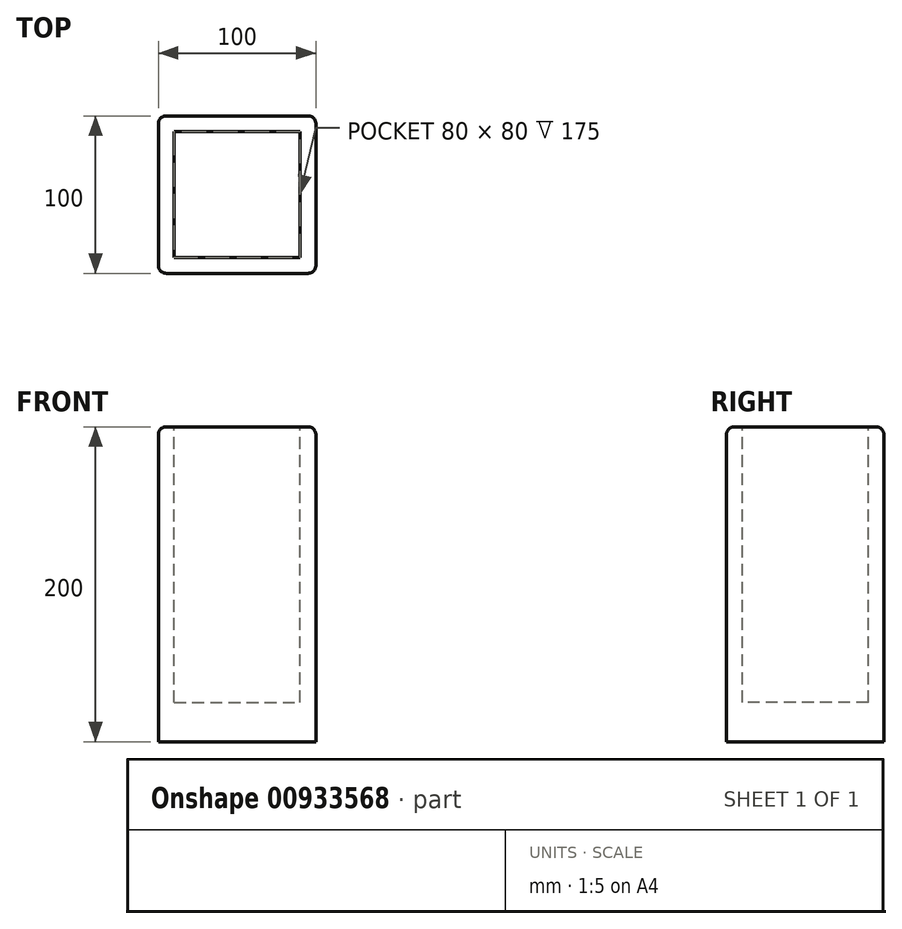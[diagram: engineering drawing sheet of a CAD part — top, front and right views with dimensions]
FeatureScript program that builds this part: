
annotation { "Feature Type Name" : "Feature", "Feature Type Description" : "" }
export const myFeature = defineFeature(function(context is Context, id is Id, definition is map)
    precondition{}
    {
        {
            var Q0;
            Q0=qCreatedBy(makeId("Top.planeOp"),FACE);
            var sketch = newSketch(context, id + "F0", { "sketchPlane" : qUnion([Q0])});
            skLineSegment(sketch, "E0.bottom", {"start": v(-50, 50) * mm, "end": v(50, 50) * mm});
            skLineSegment(sketch, "E0.top", {"start": v(-50, -50) * mm, "end": v(50, -50) * mm});
            skLineSegment(sketch, "E0.left", {"start": v(-50, 50) * mm, "end": v(-50, -50) * mm});
            skLineSegment(sketch, "E0.right", {"start": v(50, 50) * mm, "end": v(50, -50) * mm});
            skSolve(sketch);
        }
        {
            var Q0;
            Q0 = qSketchRegion(id + "F0", true);
            var Q1;
            Q1=makeQuery(id+"F0.imprint","IMPRINT",FACE,{"disambiguationData":[TD([[makeQuery(id+"F0.imprint","IMPRINT",EDGE,{"derivedFrom":sQuery(id+"F0.wireOp",EDGE,"E0.bottom")}),-1.0]])]});
            extrude(context, id + "F1", {"entities" : qUnion([Q0, Q1]), "depth" : 200 * mm, "offsetDistance" : 25 * mm});
        }
        {
            var Q0;
            Q0=makeQuery(id+"F1.opExtrude","CAP_FACE",FACE,{"disambiguationData":[OSD([sQuery(id+"F0.wireOp",EDGE,"E0.bottom"),sQuery(id+"F0.wireOp",EDGE,"E0.top"),sQuery(id+"F0.wireOp",EDGE,"E0.left"),sQuery(id+"F0.wireOp",EDGE,"E0.right")])],"isStart":false});
            var sketch = newSketch(context, id + "F2", { "sketchPlane" : qUnion([Q0])});
            skLineSegment(sketch, "E1.bottom", {"start": v(-40, 40) * mm, "end": v(40, 40) * mm});
            skLineSegment(sketch, "E1.top", {"start": v(-40, -40) * mm, "end": v(40, -40) * mm});
            skLineSegment(sketch, "E1.left", {"start": v(-40, 40) * mm, "end": v(-40, -40) * mm});
            skLineSegment(sketch, "E1.right", {"start": v(40, 40) * mm, "end": v(40, -40) * mm});
            skPoint(sketch, "E1.middle", {"position": v(0, 0) * mm});
            skSolve(sketch);
        }
        {
            var Q0;
            Q0 = qSketchRegion(id + "F2", true);
            extrude(context, id + "F3", {"entities" : qUnion([Q0]), "operationType" : NewBodyOperationType.REMOVE, "oppositeDirection" : true, "depth" : 175 * mm, "offsetDistance" : 25 * mm});
        }
        {
            var Q0;
            Q0=makeQuery(id+"F1.opExtrude","CAP_EDGE",EDGE,{"disambiguationData":[OSD([sQuery(id+"F0.wireOp",EDGE,"E0.left")])],"isStart":false});
            var Q1;
            Q1=makeQuery(id+"F1.opExtrude","CAP_EDGE",EDGE,{"disambiguationData":[OSD([sQuery(id+"F0.wireOp",EDGE,"E0.top")])],"isStart":false});
            var Q2;
            Q2=makeQuery(id+"F1.opExtrude","CAP_EDGE",EDGE,{"disambiguationData":[OSD([sQuery(id+"F0.wireOp",EDGE,"E0.right")])],"isStart":false});
            var Q3;
            Q3=makeQuery(id+"F1.opExtrude","CAP_EDGE",EDGE,{"disambiguationData":[OSD([sQuery(id+"F0.wireOp",EDGE,"E0.bottom")])],"isStart":false});
            var Q4;
            Q4=makeQuery(id+"F3.boolean.opBoolean","COPY",EDGE,{"derivedFrom":makeQuery(id+"F3.opExtrude","CAP_EDGE",EDGE,{"disambiguationData":[OSD([sQuery(id+"F2.wireOp",EDGE,"E1.bottom")])],"isStart":true})});
            var Q5;
            Q5=makeQuery(id+"F3.boolean.opBoolean","COPY",EDGE,{"derivedFrom":makeQuery(id+"F3.opExtrude","CAP_EDGE",EDGE,{"disambiguationData":[OSD([sQuery(id+"F2.wireOp",EDGE,"E1.left")])],"isStart":true})});
            var Q6;
            Q6=makeQuery(id+"F3.boolean.opBoolean","COPY",EDGE,{"derivedFrom":makeQuery(id+"F3.opExtrude","CAP_EDGE",EDGE,{"disambiguationData":[OSD([sQuery(id+"F2.wireOp",EDGE,"E1.top")])],"isStart":true})});
            var Q7;
            Q7=makeQuery(id+"F3.boolean.opBoolean","COPY",EDGE,{"derivedFrom":makeQuery(id+"F3.opExtrude","CAP_EDGE",EDGE,{"disambiguationData":[OSD([sQuery(id+"F2.wireOp",EDGE,"E1.right")])],"isStart":true})});
            fillet(context, id + "F4", {"entities" : qUnion([Q0, Q1, Q2, Q3, Q4, Q5, Q6, Q7]), "radius" : 5 * mm, "tangentPropagation" : true, "allowEdgeOverflow" : false});
        }
        {
            var Q0;
            Q0=makeQuery(id+"F1.opExtrude","SWEPT_EDGE",EDGE,{"disambiguationData":[OSD([sQuery(id+"F0.wireOp",EDGE,"E0.top"),sQuery(id+"F0.wireOp",EDGE,"E0.right")])]});
            var Q1;
            Q1=makeQuery(id+"F1.opExtrude","SWEPT_EDGE",EDGE,{"disambiguationData":[OSD([sQuery(id+"F0.wireOp",EDGE,"E0.bottom"),sQuery(id+"F0.wireOp",EDGE,"E0.right")])]});
            var Q2;
            Q2=makeQuery(id+"F1.opExtrude","SWEPT_EDGE",EDGE,{"disambiguationData":[OSD([sQuery(id+"F0.wireOp",EDGE,"E0.top"),sQuery(id+"F0.wireOp",EDGE,"E0.left")])]});
            var Q3;
            Q3=makeQuery(id+"F1.opExtrude","SWEPT_EDGE",EDGE,{"disambiguationData":[OSD([sQuery(id+"F0.wireOp",EDGE,"E0.bottom"),sQuery(id+"F0.wireOp",EDGE,"E0.left")])]});
            fillet(context, id + "F5", {"entities" : qUnion([Q0, Q1, Q2, Q3]), "radius" : 5 * mm, "tangentPropagation" : true, "allowEdgeOverflow" : false});
        }
    });
